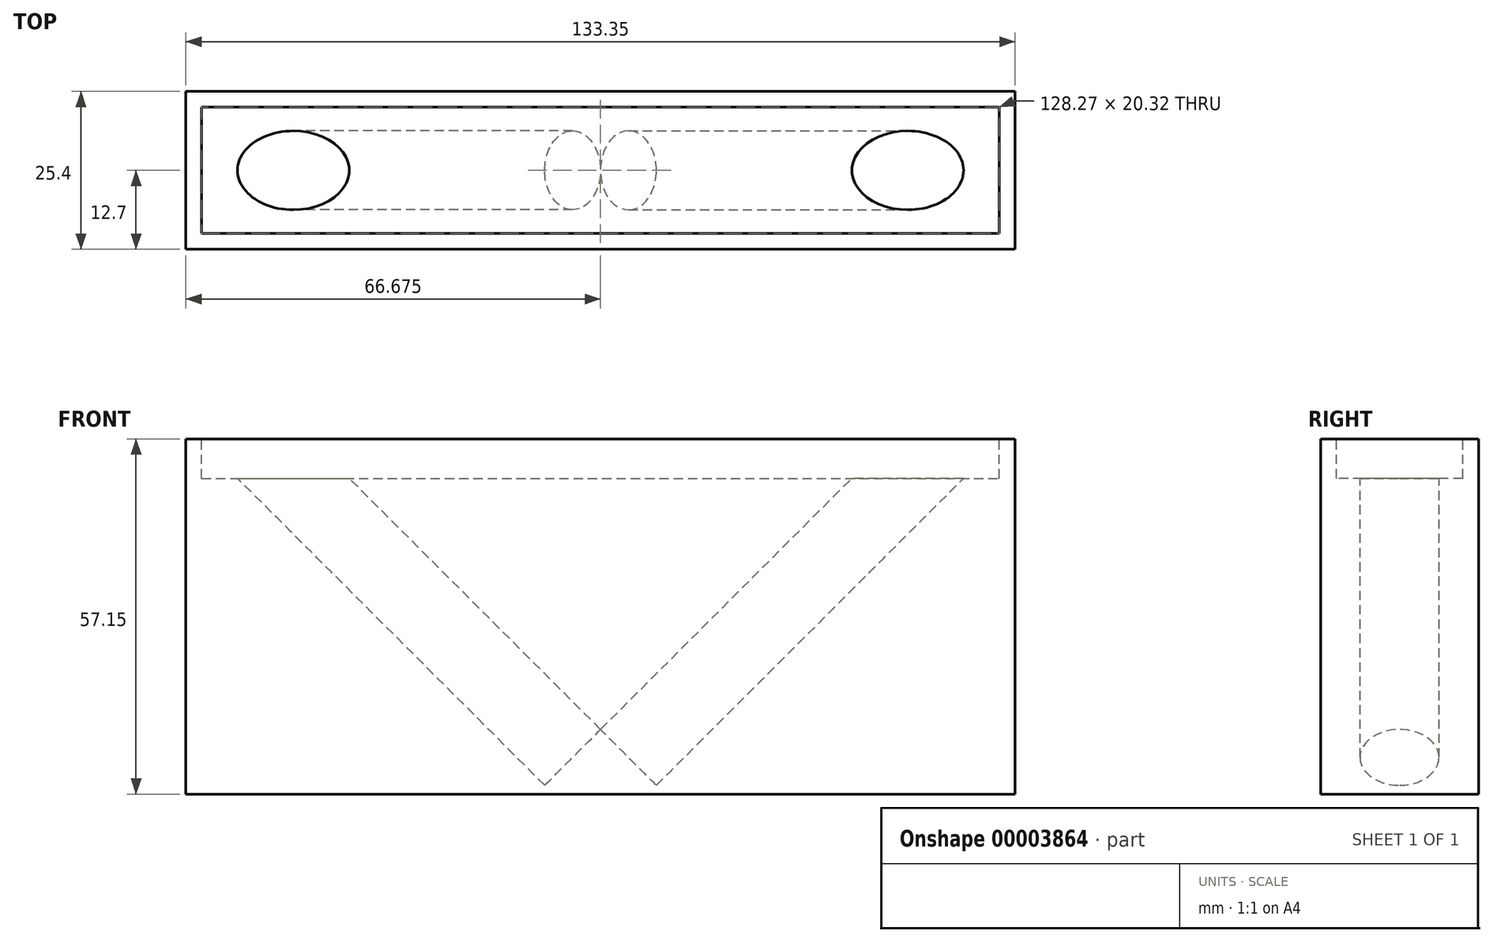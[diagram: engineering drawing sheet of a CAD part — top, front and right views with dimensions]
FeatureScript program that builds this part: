
annotation { "Feature Type Name" : "Feature", "Feature Type Description" : "" }
export const myFeature = defineFeature(function(context is Context, id is Id, definition is map)
    precondition{}
    {
        {
            var Q0;
            Q0=qCreatedBy(makeId("Front.planeOp"),FACE);
            var sketch = newSketch(context, id + "F0", { "sketchPlane" : qUnion([Q0])});
            skLineSegment(sketch, "E0", {"start": v(0, 0) * mm, "end": v(133.35, 0) * mm});
            skLineSegment(sketch, "E1", {"start": v(133.35, 57.15) * mm, "end": v(133.35, 0) * mm});
            skLineSegment(sketch, "E2", {"start": v(0, 57.15) * mm, "end": v(0, 0) * mm});
            skLineSegment(sketch, "E3", {"start": v(0, 57.15) * mm, "end": v(133.35, 57.15) * mm});
            skSolve(sketch);
        }
        {
            var Q0;
            Q0 = qSketchRegion(id + "F0", true);
            extrude(context, id + "F1", {"entities" : qUnion([Q0]), "endBound" : BoundingType.SYMMETRIC, "depth" : 25.4 * mm});
        }
        {
            var Q0;
            Q0=makeQuery(id+"F1.opExtrude","SWEPT_FACE",FACE,{"disambiguationData":[OSD([sQuery(id+"F0.wireOp",EDGE,"E3")])]});
            var sketch = newSketch(context, id + "F2", { "sketchPlane" : qUnion([Q0])});
            skLineSegment(sketch, "E4.rect.bottom", {"start": v(130.81, 10.16) * mm, "end": v(2.54, 10.16) * mm});
            skLineSegment(sketch, "E4.rect.top", {"start": v(130.81, -10.16) * mm, "end": v(2.54, -10.16) * mm});
            skLineSegment(sketch, "E4.rect.left", {"start": v(130.81, 10.16) * mm, "end": v(130.81, -10.16) * mm});
            skLineSegment(sketch, "E4.rect.right", {"start": v(2.54, 10.16) * mm, "end": v(2.54, -10.16) * mm});
            skPoint(sketch, "E4.rect.middle", {"position": v(66.68, 0) * mm});
            skLineSegment(sketch, "E5", {"start": v(0, 0) * mm, "end": v(2.54, 0) * mm, "construction": true});
            skLineSegment(sketch, "E6", {"start": v(66.68, 10.16) * mm, "end": v(66.68, 12.7) * mm, "construction": true});
            skSolve(sketch);
        }
        {
            var Q0;
            Q0 = qSketchRegion(id + "F2", true);
            extrude(context, id + "F3", {"entities" : qUnion([Q0]), "operationType" : NewBodyOperationType.REMOVE, "oppositeDirection" : true, "depth" : 6.35 * mm});
        }
        {
            var Q0;
            Q0=qCreatedBy(makeId("Front.planeOp"),FACE);
            var sketch = newSketch(context, id + "F4", { "sketchPlane" : qUnion([Q0])});
            skLineSegment(sketch, "E7", {"start": v(116.07, 59.78) * mm, "end": v(66.67, 10.39) * mm});
            skLineSegment(sketch, "E8", {"start": v(66.67, 10.39) * mm, "end": v(71.17, 5.9) * mm});
            skLineSegment(sketch, "E9", {"start": v(71.17, 5.9) * mm, "end": v(120.56, 55.3) * mm});
            skLineSegment(sketch, "E10", {"start": v(71.17, 5.9) * mm, "end": v(75.66, 1.4) * mm, "construction": true});
            skLineSegment(sketch, "E11", {"start": v(75.66, 1.4) * mm, "end": v(125.05, 50.8) * mm, "construction": true});
            skLineSegment(sketch, "E12", {"start": v(125.05, 50.8) * mm, "end": v(120.56, 55.3) * mm, "construction": true});
            skLineSegment(sketch, "E13", {"start": v(66.68, 10.39) * mm, "end": v(66.68, 0) * mm, "construction": true});
            skLineSegment(sketch, "E14", {"start": v(120.56, 55.3) * mm, "end": v(116.07, 59.78) * mm});
            skLineSegment(sketch, "E15", {"start": v(66.68, 0) * mm, "end": v(133.35, 0) * mm});
            skLineSegment(sketch, "E16", {"start": v(66.68, 0) * mm, "end": v(0, 0) * mm});
            skSolve(sketch);
        }
        {
            var Q0;
            Q0 = qSketchRegion(id + "F4", true);
            var Q1;
            Q1=sQuery(id+"F4.wireOp",EDGE,"E9");
            revolve(context, id + "F5", {"operationType" : NewBodyOperationType.REMOVE, "entities" : qUnion([Q0]), "axis" : qUnion([Q1]), "revolveType" : RevolveType.FULL, "oppositeDirection" : true});
        }
        {
            var Q0;
            Q0=makeQuery(id+"F1.opExtrude","SWEPT_FACE",FACE,{"disambiguationData":[OSD([sQuery(id+"F0.wireOp",EDGE,"E1")])]});
            var Q1;
            Q1=makeQuery(id+"F1.opExtrude","SWEPT_FACE",FACE,{"disambiguationData":[OSD([sQuery(id+"F0.wireOp",EDGE,"E2")])]});
            cPlane(context, id + "F6", {"entities" : qUnion([Q0, Q1]), "cplaneType" : CPlaneType.MID_PLANE, "offset" : 152.4 * mm, "width" : 152.4 * mm, "height" : 152.4 * mm});
        }
        {
            var Q0;
            Q0=makeQuery(id+"F1.opExtrude","SWEPT_BODY",BODY,{"disambiguationData":[OSD([sQuery(id+"F0.wireOp",EDGE,"E0"),sQuery(id+"F0.wireOp",EDGE,"E1"),sQuery(id+"F0.wireOp",EDGE,"E2"),sQuery(id+"F0.wireOp",EDGE,"E3")])]});
            var Q1;
            Q1=qCreatedBy(id+"F6.planeOp",FACE);
            mirror(context, id + "F7", {"entities" : qUnion([Q0]), "mirrorPlane" : qUnion([Q1])});
        }
    });
